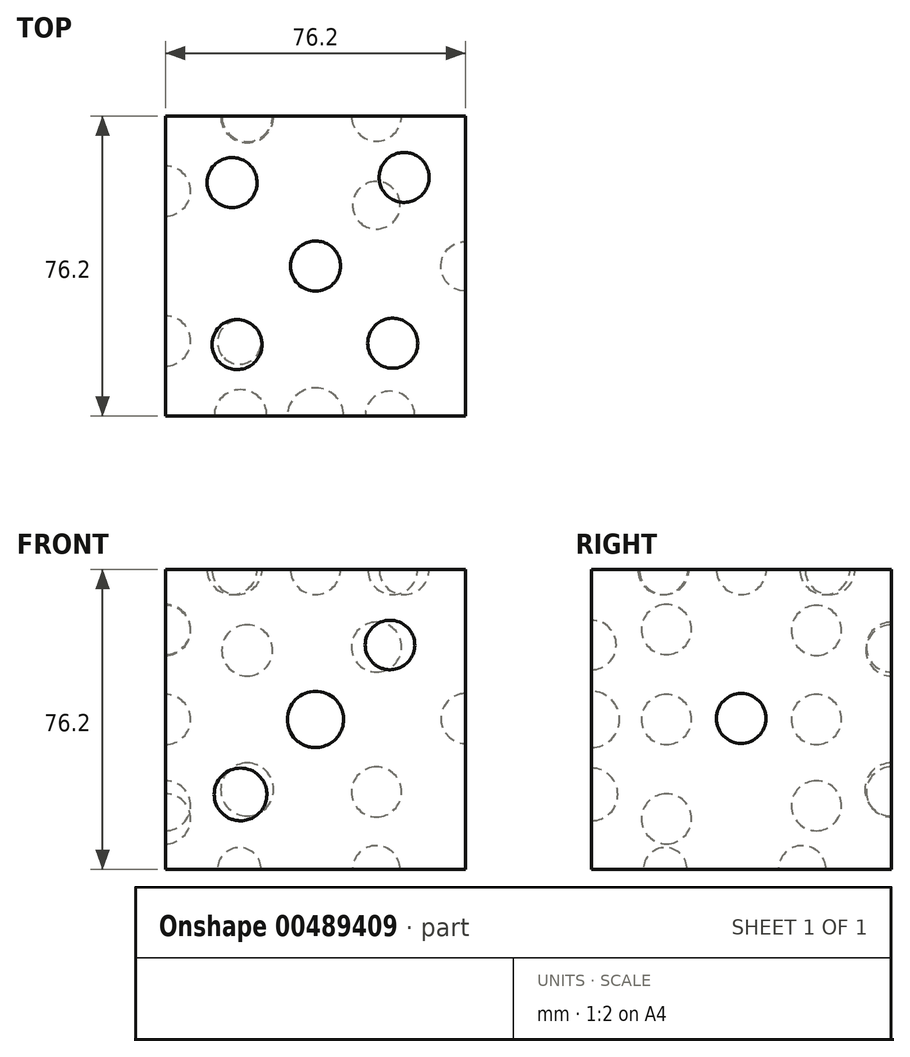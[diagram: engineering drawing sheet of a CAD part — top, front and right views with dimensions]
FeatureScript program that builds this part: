
annotation { "Feature Type Name" : "Feature", "Feature Type Description" : "" }
export const myFeature = defineFeature(function(context is Context, id is Id, definition is map)
    precondition{}
    {
        {
            var Q0;
            Q0=qCreatedBy(makeId("Front.planeOp"),FACE);
            var sketch = newSketch(context, id + "F0", { "sketchPlane" : qUnion([Q0])});
            skLineSegment(sketch, "E0.bottom", {"start": v(1.97, 0) * mm, "end": v(78.17, 0) * mm});
            skLineSegment(sketch, "E0.top", {"start": v(1.97, 76.2) * mm, "end": v(78.17, 76.2) * mm});
            skLineSegment(sketch, "E0.left", {"start": v(1.97, 0) * mm, "end": v(1.97, 76.2) * mm});
            skLineSegment(sketch, "E0.right", {"start": v(78.17, 0) * mm, "end": v(78.17, 76.2) * mm});
            skSolve(sketch);
        }
        {
            var Q0;
            Q0 = qSketchRegion(id + "F0", true);
            extrude(context, id + "F1", {"entities" : qUnion([Q0]), "depth" : 76.2 * mm});
        }
        {
            var Q0;
            Q0=makeQuery(id+"F1.opExtrude","SWEPT_FACE",FACE,{"disambiguationData":[OSD([sQuery(id+"F0.wireOp",EDGE,"E0.right")])]});
            var sketch = newSketch(context, id + "F2", { "sketchPlane" : qUnion([Q0])});
            skArc(sketch, "E1", {"start": v(-38.18, 32) * mm, "mid": v(-31.88, 38.34) * mm, "end": v(-38.15, 44.7) * mm});
            skLineSegment(sketch, "E2", {"start": v(-38.1, 76.2) * mm, "end": v(-38.23, 0) * mm});
            skSolve(sketch);
        }
        {
            var Q0;
            {var subQ0=sQuery(id+"F2.wireOp",EDGE,"E1");Q0=makeQuery(id+"F2.imprint","IMPRINT",FACE,{"disambiguationData":[TD([[makeQuery(id+"F2.imprint","IMPRINT",EDGE,{"derivedFrom":subQ0}),1.0]])]});}
            var Q1;
            Q1=sQuery(id+"F2.wireOp",EDGE,"E2");
            revolve(context, id + "F3", {"operationType" : NewBodyOperationType.REMOVE, "entities" : qUnion([Q0]), "axis" : qUnion([Q1]), "revolveType" : RevolveType.FULL});
        }
        {
            var Q0;
            Q0=makeQuery(id+"F1.opExtrude","SWEPT_FACE",FACE,{"disambiguationData":[OSD([sQuery(id+"F0.wireOp",EDGE,"E0.left")])]});
            var sketch = newSketch(context, id + "F4", { "sketchPlane" : qUnion([Q0])});
            skLineSegment(sketch, "E3", {"start": v(0, 76.2) * mm, "end": v(38.1, 76.2) * mm});
            skLineSegment(sketch, "E4", {"start": v(19.05, 67.08) * mm, "end": v(19.05, 54.38) * mm});
            skLineSegment(sketch, "E5", {"start": v(38.1, 76.2) * mm, "end": v(76.2, 76.2) * mm});
            skLineSegment(sketch, "E6", {"start": v(57.15, 67.3) * mm, "end": v(57.15, 54.6) * mm});
            skArc(sketch, "E7", {"start": v(19.05, 54.38) * mm, "mid": v(25.4, 60.73) * mm, "end": v(19.05, 67.08) * mm});
            skArc(sketch, "E8", {"start": v(19.05, 31.75) * mm, "mid": v(25.4, 38.1) * mm, "end": v(19.05, 44.45) * mm});
            skArc(sketch, "E9", {"start": v(19.05, 9.83) * mm, "mid": v(25.4, 16.18) * mm, "end": v(19.05, 22.53) * mm});
            skArc(sketch, "E10", {"start": v(57.15, 54.6) * mm, "mid": v(63.5, 60.95) * mm, "end": v(57.15, 67.3) * mm});
            skArc(sketch, "E11", {"start": v(57.15, 31.75) * mm, "mid": v(63.5, 38.1) * mm, "end": v(57.15, 44.45) * mm});
            skArc(sketch, "E12", {"start": v(57.15, 6.5) * mm, "mid": v(63.5, 12.85) * mm, "end": v(57.15, 19.2) * mm});
            skPoint(sketch, "E13.orphan", {"position": v(19.05, 76.2) * mm});
            skLineSegment(sketch, "E14.trimOffspring", {"start": v(19.05, 44.45) * mm, "end": v(19.05, 31.75) * mm});
            skLineSegment(sketch, "E15.trimOffspring", {"start": v(19.05, 22.53) * mm, "end": v(19.05, 9.83) * mm});
            skPoint(sketch, "E16.orphan", {"position": v(19.05, 0) * mm});
            skPoint(sketch, "E17.orphan", {"position": v(57.15, 0) * mm});
            skLineSegment(sketch, "E18.trimOffspring", {"start": v(57.15, 19.2) * mm, "end": v(57.15, 6.5) * mm});
            skLineSegment(sketch, "E19.trimOffspring", {"start": v(57.15, 44.45) * mm, "end": v(57.15, 31.75) * mm});
            skPoint(sketch, "E20.orphan", {"position": v(57.15, 76.2) * mm});
            skSolve(sketch);
        }
        {
            var Q0;
            Q0=makeQuery(id+"F4.imprint","IMPRINT",FACE,{"disambiguationData":[TD([[makeQuery(id+"F4.imprint","IMPRINT",EDGE,{"derivedFrom":sQuery(id+"F4.wireOp",EDGE,"E4")}),1.0]])]});
            var Q1;
            Q1=makeQuery(id+"F4.imprint","IMPRINT",FACE,{"disambiguationData":[TD([[makeQuery(id+"F4.imprint","IMPRINT",EDGE,{"derivedFrom":sQuery(id+"F4.wireOp",EDGE,"E8")}),1.0]])]});
            var Q2;
            Q2=makeQuery(id+"F4.imprint","IMPRINT",FACE,{"disambiguationData":[TD([[makeQuery(id+"F4.imprint","IMPRINT",EDGE,{"derivedFrom":sQuery(id+"F4.wireOp",EDGE,"E9")}),1.0]])]});
            var Q3;
            Q3=sQuery(id+"F4.wireOp",EDGE,"E4");
            revolve(context, id + "F5", {"operationType" : NewBodyOperationType.REMOVE, "entities" : qUnion([Q0, Q1, Q2]), "axis" : qUnion([Q3]), "revolveType" : RevolveType.FULL, "oppositeDirection" : true});
        }
        {
            var Q0;
            Q0=makeQuery(id+"F4.imprint","IMPRINT",FACE,{"disambiguationData":[TD([[makeQuery(id+"F4.imprint","IMPRINT",EDGE,{"derivedFrom":sQuery(id+"F4.wireOp",EDGE,"E6")}),1.0]])]});
            var Q1;
            Q1=makeQuery(id+"F4.imprint","IMPRINT",FACE,{"disambiguationData":[TD([[makeQuery(id+"F4.imprint","IMPRINT",EDGE,{"derivedFrom":sQuery(id+"F4.wireOp",EDGE,"E11")}),1.0]])]});
            var Q2;
            Q2=makeQuery(id+"F4.imprint","IMPRINT",FACE,{"disambiguationData":[TD([[makeQuery(id+"F4.imprint","IMPRINT",EDGE,{"derivedFrom":sQuery(id+"F4.wireOp",EDGE,"E12")}),1.0]])]});
            var Q3;
            Q3=sQuery(id+"F4.wireOp",EDGE,"E6");
            revolve(context, id + "F6", {"operationType" : NewBodyOperationType.REMOVE, "entities" : qUnion([Q0, Q1, Q2]), "axis" : qUnion([Q3]), "revolveType" : RevolveType.FULL, "oppositeDirection" : true});
        }
        {
            var Q0;
            Q0=makeQuery(id+"F1.opExtrude","CAP_FACE",FACE,{"disambiguationData":[OSD([sQuery(id+"F0.wireOp",EDGE,"E0.bottom"),sQuery(id+"F0.wireOp",EDGE,"E0.top"),sQuery(id+"F0.wireOp",EDGE,"E0.left"),sQuery(id+"F0.wireOp",EDGE,"E0.right")])],"isStart":false});
            var sketch = newSketch(context, id + "F7", { "sketchPlane" : qUnion([Q0])});
            skLineSegment(sketch, "E21", {"start": v(63.44, 61.47) * mm, "end": v(54.54, 52.57) * mm});
            skLineSegment(sketch, "E22", {"start": v(16.29, 14.32) * mm, "end": v(25.75, 23.78) * mm});
            skLineSegment(sketch, "E23", {"start": v(40.07, 38.1) * mm, "end": v(35.02, 33.05) * mm});
            skLineSegment(sketch, "E24", {"start": v(40.07, 38.1) * mm, "end": v(45.12, 43.15) * mm});
            skArc(sketch, "E25", {"start": v(16.29, 14.32) * mm, "mid": v(25.75, 14.32) * mm, "end": v(25.75, 23.78) * mm});
            skArc(sketch, "E26", {"start": v(35.02, 33.05) * mm, "mid": v(45.12, 33.05) * mm, "end": v(45.12, 43.15) * mm});
            skArc(sketch, "E27", {"start": v(54.54, 52.57) * mm, "mid": v(63.44, 52.57) * mm, "end": v(63.44, 61.47) * mm});
            skLineSegment(sketch, "E28.trimOffspring", {"start": v(54.54, 52.57) * mm, "end": v(59, 57.02) * mm});
            skLineSegment(sketch, "E29.trimOffspring", {"start": v(25.75, 23.78) * mm, "end": v(21.02, 19.05) * mm});
            skPoint(sketch, "E30.orphan", {"position": v(1.97, 0) * mm});
            skLineSegment(sketch, "E31.trimOffspring", {"start": v(35.02, 33.05) * mm, "end": v(40.07, 38.1) * mm});
            skLineSegment(sketch, "E32.trimOffspring", {"start": v(45.12, 43.15) * mm, "end": v(35.02, 33.05) * mm});
            skLineSegment(sketch, "E33.trimOffspring", {"start": v(25.75, 23.78) * mm, "end": v(16.29, 14.32) * mm});
            skPoint(sketch, "E34.orphan", {"position": v(78.17, 76.2) * mm});
            skSolve(sketch);
        }
        {
            var Q0;
            {var subQ0=sQuery(id+"F7.wireOp",EDGE,"E25");Q0=makeQuery(id+"F7.imprint","IMPRINT",FACE,{"disambiguationData":[TD([[makeQuery(id+"F7.imprint","IMPRINT",EDGE,{"derivedFrom":subQ0}),1.0]])]});}
            var Q1;
            {var subQ0=sQuery(id+"F7.wireOp",EDGE,"E26");Q1=makeQuery(id+"F7.imprint","IMPRINT",FACE,{"disambiguationData":[TD([[makeQuery(id+"F7.imprint","IMPRINT",EDGE,{"derivedFrom":subQ0}),1.0]])]});}
            var Q2;
            Q2=makeQuery(id+"F7.imprint","IMPRINT",FACE,{"disambiguationData":[TD([[makeQuery(id+"F7.imprint","IMPRINT",EDGE,{"derivedFrom":sQuery(id+"F7.wireOp",EDGE,"E21")}),1.0]])]});
            var Q3;
            Q3=sQuery(id+"F7.wireOp",EDGE,"E33.trimOffspring");
            revolve(context, id + "F8", {"operationType" : NewBodyOperationType.REMOVE, "entities" : qUnion([Q0, Q1, Q2]), "axis" : qUnion([Q3]), "revolveType" : RevolveType.FULL, "oppositeDirection" : true});
        }
        {
            var Q0;
            Q0=makeQuery(id+"F1.opExtrude","CAP_FACE",FACE,{"disambiguationData":[OSD([sQuery(id+"F0.wireOp",EDGE,"E0.bottom"),sQuery(id+"F0.wireOp",EDGE,"E0.top"),sQuery(id+"F0.wireOp",EDGE,"E0.left"),sQuery(id+"F0.wireOp",EDGE,"E0.right")])],"isStart":true});
            var sketch = newSketch(context, id + "F9", { "sketchPlane" : qUnion([Q0])});
            skLineSegment(sketch, "E35", {"start": v(-58.06, 62.42) * mm, "end": v(-58.06, 48.88) * mm});
            skLineSegment(sketch, "E36", {"start": v(-58.06, 15.3) * mm, "end": v(-58.06, 30.29) * mm});
            skLineSegment(sketch, "E37", {"start": v(-22.71, 62.13) * mm, "end": v(-22.71, 49.18) * mm});
            skArc(sketch, "E38", {"start": v(-58.06, 48.88) * mm, "mid": v(-51.3, 55.65) * mm, "end": v(-58.06, 62.42) * mm});
            skArc(sketch, "E39", {"start": v(-58.06, 15.3) * mm, "mid": v(-50.57, 22.8) * mm, "end": v(-58.06, 30.29) * mm});
            skArc(sketch, "E40", {"start": v(-22.71, 49.18) * mm, "mid": v(-16.23, 55.65) * mm, "end": v(-22.71, 62.13) * mm});
            skArc(sketch, "E41", {"start": v(-22.71, 13.57) * mm, "mid": v(-15.98, 20.3) * mm, "end": v(-22.71, 27.04) * mm});
            skLineSegment(sketch, "E42.trimOffspring", {"start": v(-22.71, 27.04) * mm, "end": v(-22.71, 13.57) * mm});
            skPoint(sketch, "E43.orphan", {"position": v(-22.71, 0) * mm});
            skLineSegment(sketch, "E44.trimOffspring", {"start": v(-58.06, 48.88) * mm, "end": v(-58.06, 62.42) * mm});
            skPoint(sketch, "E45.orphan", {"position": v(-58.06, 0) * mm});
            skLineSegment(sketch, "E46.trimOffspring", {"start": v(-58.06, 30.29) * mm, "end": v(-58.06, 15.3) * mm});
            skSolve(sketch);
        }
        {
            var Q0;
            Q0=makeQuery(id+"F9.imprint","IMPRINT",FACE,{"disambiguationData":[TD([[makeQuery(id+"F9.imprint","IMPRINT",EDGE,{"derivedFrom":sQuery(id+"F9.wireOp",EDGE,"E37")}),1.0]])]});
            var Q1;
            Q1=makeQuery(id+"F9.imprint","IMPRINT",FACE,{"disambiguationData":[TD([[makeQuery(id+"F9.imprint","IMPRINT",EDGE,{"derivedFrom":sQuery(id+"F9.wireOp",EDGE,"E41")}),1.0]])]});
            var Q2;
            Q2=sQuery(id+"F9.wireOp",EDGE,"E37");
            revolve(context, id + "F10", {"operationType" : NewBodyOperationType.REMOVE, "entities" : qUnion([Q0, Q1]), "axis" : qUnion([Q2]), "revolveType" : RevolveType.FULL, "oppositeDirection" : true});
        }
        {
            var Q0;
            Q0=makeQuery(id+"F1.opExtrude","CAP_FACE",FACE,{"disambiguationData":[OSD([sQuery(id+"F0.wireOp",EDGE,"E0.bottom"),sQuery(id+"F0.wireOp",EDGE,"E0.top"),sQuery(id+"F0.wireOp",EDGE,"E0.left"),sQuery(id+"F0.wireOp",EDGE,"E0.right")])],"isStart":true});
            var sketch = newSketch(context, id + "F11", { "sketchPlane" : qUnion([Q0])});
            skLineSegment(sketch, "E47", {"start": v(-55.57, 62.83) * mm, "end": v(-55.57, 50.13) * mm});
            skArc(sketch, "E48", {"start": v(-55.57, 50.13) * mm, "mid": v(-49.22, 56.48) * mm, "end": v(-55.57, 62.83) * mm});
            skArc(sketch, "E49", {"start": v(-55.57, 13.33) * mm, "mid": v(-49.22, 19.68) * mm, "end": v(-55.57, 26.03) * mm});
            skLineSegment(sketch, "E50.trimOffspring", {"start": v(-55.57, 26.03) * mm, "end": v(-55.57, 13.33) * mm});
            skPoint(sketch, "E51.orphan", {"position": v(-55.57, 0) * mm});
            skSolve(sketch);
        }
        {
            var Q0;
            Q0=makeQuery(id+"F11.imprint","IMPRINT",FACE,{"disambiguationData":[TD([[makeQuery(id+"F11.imprint","IMPRINT",EDGE,{"derivedFrom":sQuery(id+"F11.wireOp",EDGE,"E47")}),1.0]])]});
            var Q1;
            Q1=makeQuery(id+"F11.imprint","IMPRINT",FACE,{"disambiguationData":[TD([[makeQuery(id+"F11.imprint","IMPRINT",EDGE,{"derivedFrom":sQuery(id+"F11.wireOp",EDGE,"E49")}),1.0]])]});
            var Q2;
            Q2=sQuery(id+"F11.wireOp",EDGE,"E47");
            revolve(context, id + "F12", {"operationType" : NewBodyOperationType.REMOVE, "entities" : qUnion([Q0, Q1]), "axis" : qUnion([Q2]), "revolveType" : RevolveType.FULL, "oppositeDirection" : true});
        }
        {
            var Q0;
            Q0=makeQuery(id+"F1.opExtrude","SWEPT_FACE",FACE,{"disambiguationData":[OSD([sQuery(id+"F0.wireOp",EDGE,"E0.bottom")])]});
            var sketch = newSketch(context, id + "F13", { "sketchPlane" : qUnion([Q0])});
            skLineSegment(sketch, "E52", {"start": v(16.78, 61.4) * mm, "end": v(24.62, 53.55) * mm});
            skArc(sketch, "E53", {"start": v(24.62, 53.55) * mm, "mid": v(24.62, 61.4) * mm, "end": v(16.78, 61.4) * mm});
            skArc(sketch, "E54", {"start": v(59.79, 18.38) * mm, "mid": v(59.79, 26.92) * mm, "end": v(51.25, 26.92) * mm});
            skLineSegment(sketch, "E55.trimOffspring", {"start": v(51.25, 26.92) * mm, "end": v(59.79, 18.38) * mm});
            skSolve(sketch);
        }
        {
            var Q0;
            Q0=makeQuery(id+"F13.imprint","IMPRINT",FACE,{"disambiguationData":[TD([[makeQuery(id+"F13.imprint","IMPRINT",EDGE,{"derivedFrom":sQuery(id+"F13.wireOp",EDGE,"E52")}),1.0]])]});
            var Q1;
            Q1=makeQuery(id+"F13.imprint","IMPRINT",FACE,{"disambiguationData":[TD([[makeQuery(id+"F13.imprint","IMPRINT",EDGE,{"derivedFrom":sQuery(id+"F13.wireOp",EDGE,"E54")}),1.0]])]});
            var Q2;
            Q2=sQuery(id+"F13.wireOp",EDGE,"E52");
            revolve(context, id + "F14", {"operationType" : NewBodyOperationType.REMOVE, "entities" : qUnion([Q0, Q1]), "axis" : qUnion([Q2]), "revolveType" : RevolveType.FULL, "oppositeDirection" : true});
        }
        {
            var Q0;
            Q0=makeQuery(id+"F1.opExtrude","SWEPT_FACE",FACE,{"disambiguationData":[OSD([sQuery(id+"F0.wireOp",EDGE,"E0.top")])]});
            var sketch = newSketch(context, id + "F15", { "sketchPlane" : qUnion([Q0])});
            skLineSegment(sketch, "E56", {"start": v(14.38, -12.41) * mm, "end": v(23.36, -21.4) * mm});
            skLineSegment(sketch, "E57", {"start": v(67.08, -11.1) * mm, "end": v(58.1, -20.07) * mm});
            skArc(sketch, "E58", {"start": v(23.36, -21.4) * mm, "mid": v(23.36, -12.41) * mm, "end": v(14.38, -12.41) * mm});
            skArc(sketch, "E59", {"start": v(67.08, -11.1) * mm, "mid": v(58.1, -11.1) * mm, "end": v(58.1, -20.07) * mm});
            skArc(sketch, "E60", {"start": v(44.56, -42.6) * mm, "mid": v(44.56, -33.6) * mm, "end": v(35.58, -33.6) * mm});
            skArc(sketch, "E61", {"start": v(64.18, -62.2) * mm, "mid": v(64.18, -53.23) * mm, "end": v(55.2, -53.23) * mm});
            skArc(sketch, "E62", {"start": v(24.6, -53.56) * mm, "mid": v(15.63, -53.56) * mm, "end": v(15.63, -62.54) * mm});
            skLineSegment(sketch, "E63.trimOffspring", {"start": v(24.6, -53.56) * mm, "end": v(15.63, -62.54) * mm});
            skPoint(sketch, "E64.orphan", {"position": v(1.97, -76.2) * mm});
            skPoint(sketch, "E65.orphan", {"position": v(78.17, 0) * mm});
            skLineSegment(sketch, "E66.trimOffspring", {"start": v(55.2, -53.23) * mm, "end": v(64.18, -62.2) * mm});
            skLineSegment(sketch, "E67.trimOffspring", {"start": v(35.58, -33.6) * mm, "end": v(44.56, -42.6) * mm});
            skSolve(sketch);
        }
        {
            var Q0;
            Q0=makeQuery(id+"F15.imprint","IMPRINT",FACE,{"disambiguationData":[TD([[makeQuery(id+"F15.imprint","IMPRINT",EDGE,{"derivedFrom":sQuery(id+"F15.wireOp",EDGE,"E56")}),1.0]])]});
            var Q1;
            Q1=makeQuery(id+"F15.imprint","IMPRINT",FACE,{"disambiguationData":[TD([[makeQuery(id+"F15.imprint","IMPRINT",EDGE,{"derivedFrom":sQuery(id+"F15.wireOp",EDGE,"E60")}),1.0]])]});
            var Q2;
            Q2=makeQuery(id+"F15.imprint","IMPRINT",FACE,{"disambiguationData":[TD([[makeQuery(id+"F15.imprint","IMPRINT",EDGE,{"derivedFrom":sQuery(id+"F15.wireOp",EDGE,"E61")}),1.0]])]});
            var Q3;
            Q3=sQuery(id+"F15.wireOp",EDGE,"E56");
            revolve(context, id + "F16", {"operationType" : NewBodyOperationType.REMOVE, "entities" : qUnion([Q0, Q1, Q2]), "axis" : qUnion([Q3]), "revolveType" : RevolveType.FULL, "oppositeDirection" : true});
        }
        {
            var Q0;
            Q0=makeQuery(id+"F15.imprint","IMPRINT",FACE,{"disambiguationData":[TD([[makeQuery(id+"F15.imprint","IMPRINT",EDGE,{"derivedFrom":sQuery(id+"F15.wireOp",EDGE,"E57")}),-1.0]])]});
            var Q1;
            Q1=makeQuery(id+"F15.imprint","IMPRINT",FACE,{"disambiguationData":[TD([[makeQuery(id+"F15.imprint","IMPRINT",EDGE,{"derivedFrom":sQuery(id+"F15.wireOp",EDGE,"E62")}),1.0]])]});
            var Q2;
            Q2=sQuery(id+"F15.wireOp",EDGE,"E57");
            revolve(context, id + "F17", {"operationType" : NewBodyOperationType.REMOVE, "entities" : qUnion([Q0, Q1]), "axis" : qUnion([Q2]), "revolveType" : RevolveType.FULL, "oppositeDirection" : true});
        }
    });
